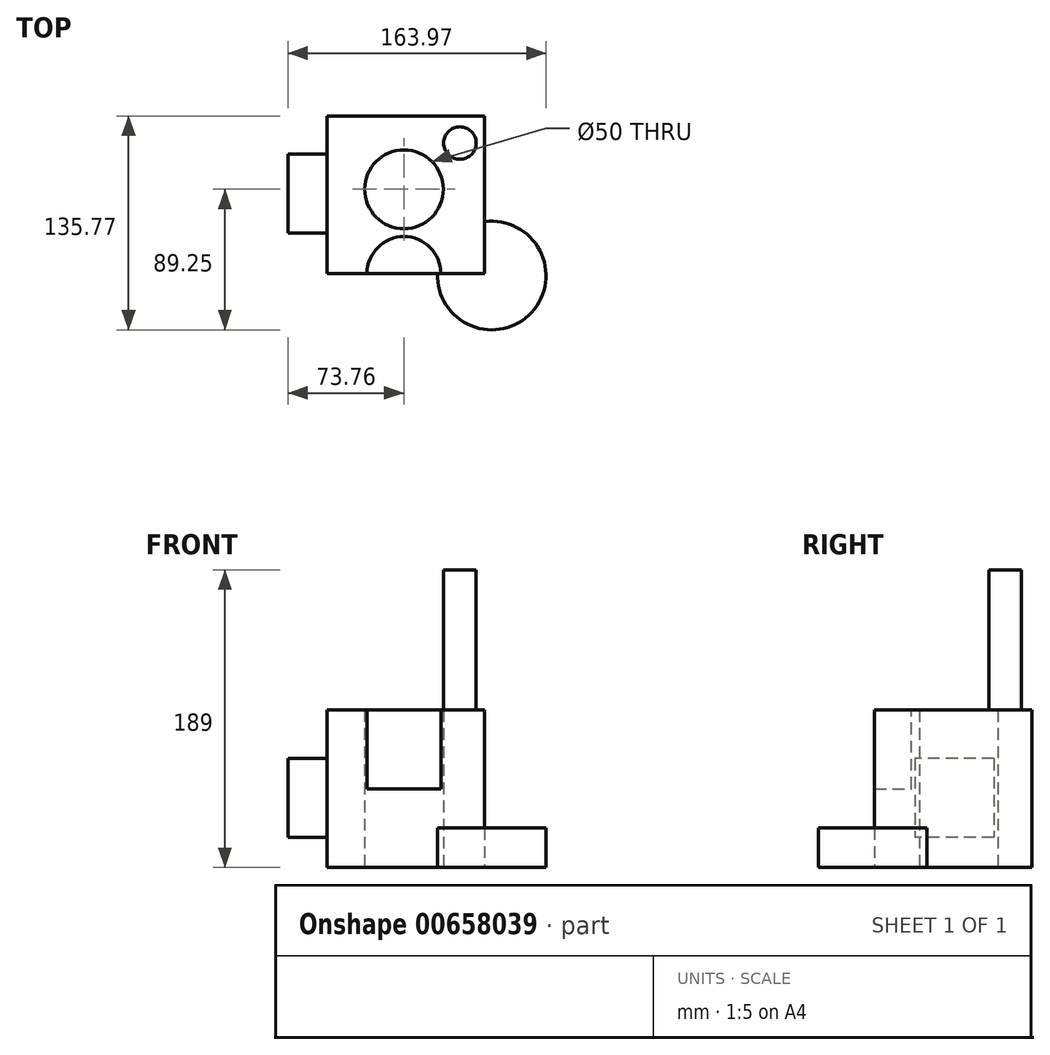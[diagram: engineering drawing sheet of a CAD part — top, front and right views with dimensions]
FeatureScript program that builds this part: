
annotation { "Feature Type Name" : "Feature", "Feature Type Description" : "" }
export const myFeature = defineFeature(function(context is Context, id is Id, definition is map)
    precondition{}
    {
        {
            var Q0;
            Q0=qCreatedBy(makeId("Top.planeOp"),FACE);
            var sketch = newSketch(context, id + "F0", { "sketchPlane" : qUnion([Q0])});
            skLineSegment(sketch, "E0.bottom", {"start": v(-48.76, 46.52) * mm, "end": v(51.24, 46.52) * mm});
            skLineSegment(sketch, "E0.top", {"start": v(-48.76, -53.48) * mm, "end": v(51.24, -53.48) * mm});
            skLineSegment(sketch, "E0.left", {"start": v(-48.76, 46.52) * mm, "end": v(-48.76, -53.48) * mm});
            skLineSegment(sketch, "E0.right", {"start": v(51.24, 46.52) * mm, "end": v(51.24, -53.48) * mm});
            skCircle(sketch, "E1", {"center": v(0, 0) * mm, "radius": 25 * mm});
            skSolve(sketch);
        }
        {
            var Q0;
            Q0 = qSketchRegion(id + "F0", true);
            extrude(context, id + "F1", {"entities" : qUnion([Q0]), "depth" : 100 * mm, "offsetDistance" : 25 * mm});
        }
        {
            var Q0;
            Q0=makeQuery(id+"F1.opExtrude","CAP_FACE",FACE,{"disambiguationData":[OSD([sQuery(id+"F0.wireOp",EDGE,"E0.bottom"),sQuery(id+"F0.wireOp",EDGE,"E0.top"),sQuery(id+"F0.wireOp",EDGE,"E0.left"),sQuery(id+"F0.wireOp",EDGE,"E0.right"),sQuery(id+"F0.wireOp",EDGE,"E1")])],"isStart":false});
            var sketch = newSketch(context, id + "F2", { "sketchPlane" : qUnion([Q0])});
            skCircle(sketch, "E2", {"center": v(0, -53.48) * mm, "radius": 23.48 * mm});
            skSolve(sketch);
        }
        {
            var Q0;
            Q0 = qSketchRegion(id + "F2", true);
            extrude(context, id + "F3", {"entities" : qUnion([Q0]), "operationType" : NewBodyOperationType.REMOVE, "oppositeDirection" : true, "depth" : 50 * mm, "offsetDistance" : 25 * mm});
        }
        {
            var Q0;
            Q0=makeQuery(id+"F1.opExtrude","SWEPT_FACE",FACE,{"disambiguationData":[OSD([sQuery(id+"F0.wireOp",EDGE,"E0.left")])]});
            var sketch = newSketch(context, id + "F4", { "sketchPlane" : qUnion([Q0])});
            skLineSegment(sketch, "E3.bottom", {"start": v(-22.33, 69.17) * mm, "end": v(27.67, 69.17) * mm});
            skLineSegment(sketch, "E3.top", {"start": v(-22.33, 19.17) * mm, "end": v(27.67, 19.17) * mm});
            skLineSegment(sketch, "E3.left", {"start": v(-22.33, 69.17) * mm, "end": v(-22.33, 19.17) * mm});
            skLineSegment(sketch, "E3.right", {"start": v(27.67, 69.17) * mm, "end": v(27.67, 19.17) * mm});
            skSolve(sketch);
        }
        {
            var Q0;
            Q0=makeQuery(id+"F4.imprint","IMPRINT",FACE,{"disambiguationData":[TD([[makeQuery(id+"F4.imprint","IMPRINT",EDGE,{"derivedFrom":sQuery(id+"F4.wireOp",EDGE,"E3.bottom")}),-1.0]])]});
            extrude(context, id + "F5", {"entities" : qUnion([Q0]), "operationType" : NewBodyOperationType.ADD, "depth" : 25 * mm, "offsetDistance" : 25 * mm});
        }
        {
            var Q0;
            Q0=qCreatedBy(makeId("Top.planeOp"),FACE);
            var sketch = newSketch(context, id + "F6", { "sketchPlane" : qUnion([Q0])});
            skCircle(sketch, "E4", {"center": v(55.73, -54.77) * mm, "radius": 34.48 * mm});
            skSolve(sketch);
        }
        {
            var Q0;
            Q0=makeQuery(id+"F6.imprint","IMPRINT",FACE,{"disambiguationData":[TD([[makeQuery(id+"F6.imprint","IMPRINT",EDGE,{"derivedFrom":sQuery(id+"F6.wireOp",EDGE,"E4")}),1.0]])]});
            extrude(context, id + "F7", {"entities" : qUnion([Q0]), "operationType" : NewBodyOperationType.ADD, "depth" : 25 * mm, "offsetDistance" : 25 * mm});
        }
        {
            var Q0;
            Q0=makeQuery(id+"F1.opExtrude","CAP_FACE",FACE,{"disambiguationData":[OSD([sQuery(id+"F0.wireOp",EDGE,"E0.bottom"),sQuery(id+"F0.wireOp",EDGE,"E0.top"),sQuery(id+"F0.wireOp",EDGE,"E0.left"),sQuery(id+"F0.wireOp",EDGE,"E0.right"),sQuery(id+"F0.wireOp",EDGE,"E1")])],"isStart":false});
            var sketch = newSketch(context, id + "F8", { "sketchPlane" : qUnion([Q0])});
            skCircle(sketch, "E5", {"center": v(35.53, 29.39) * mm, "radius": 10.32 * mm});
            skSolve(sketch);
        }
        {
            var Q0;
            Q0=makeQuery(id+"F8.imprint","IMPRINT",FACE,{"disambiguationData":[TD([[makeQuery(id+"F8.imprint","IMPRINT",EDGE,{"derivedFrom":sQuery(id+"F8.wireOp",EDGE,"E5")}),1.0]])]});
            extrude(context, id + "F9", {"entities" : qUnion([Q0]), "operationType" : NewBodyOperationType.ADD, "depth" : 89 * mm, "offsetDistance" : 25 * mm});
        }
    });
